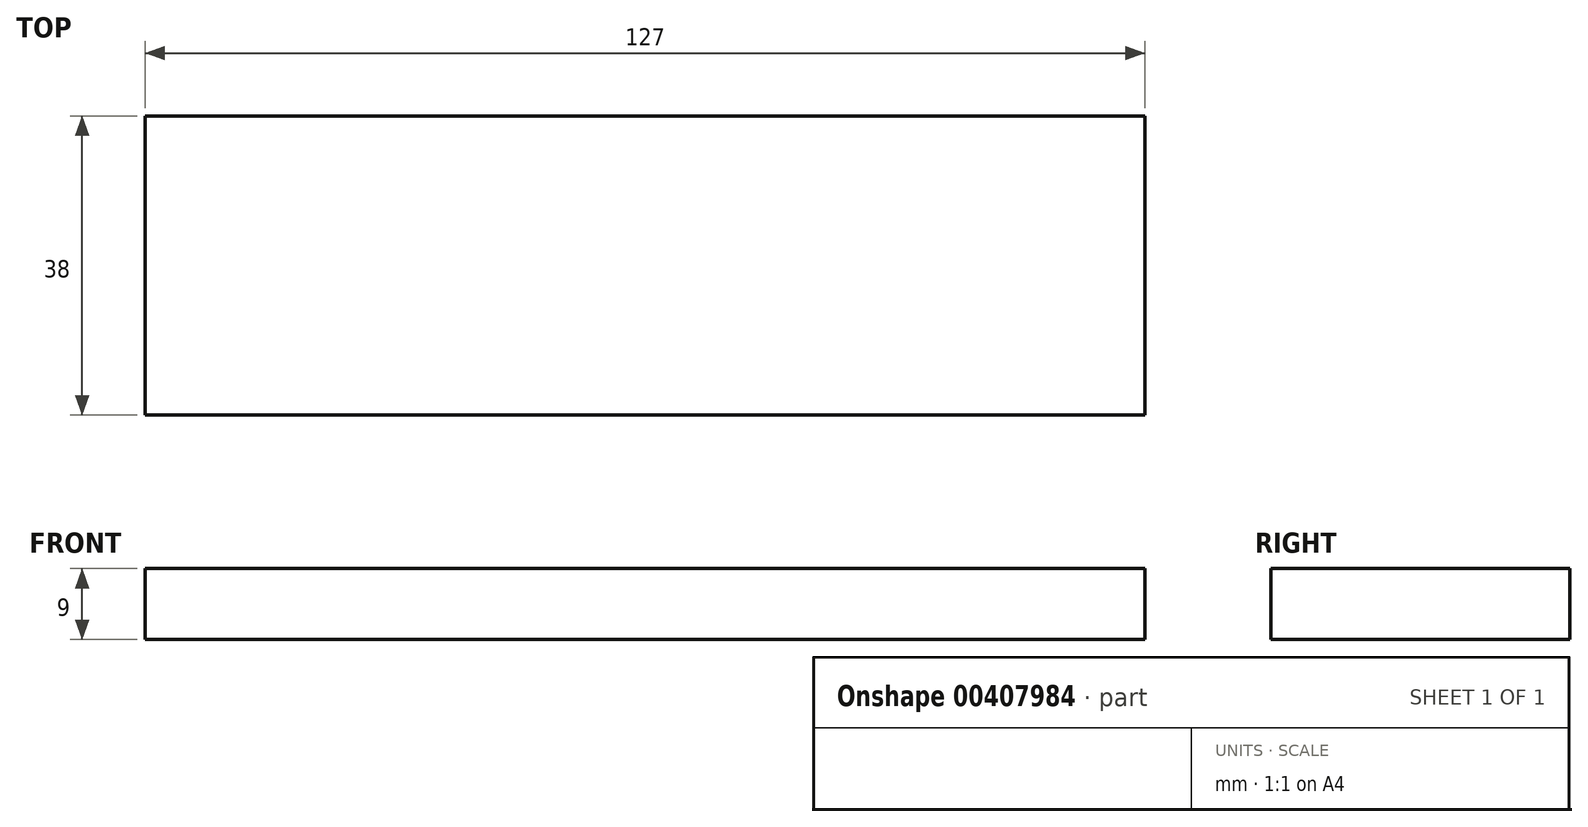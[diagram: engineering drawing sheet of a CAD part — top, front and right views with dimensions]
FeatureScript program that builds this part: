
annotation { "Feature Type Name" : "Feature", "Feature Type Description" : "" }
export const myFeature = defineFeature(function(context is Context, id is Id, definition is map)
    precondition{}
    {
        {
            var Q0;
            Q0=qCreatedBy(makeId("Top.planeOp"),FACE);
            var sketch = newSketch(context, id + "F0", { "sketchPlane" : qUnion([Q0])});
            skLineSegment(sketch, "E0.bottom", {"start": v(63.5, -19) * mm, "end": v(-63.5, -19) * mm});
            skLineSegment(sketch, "E0.top", {"start": v(63.5, 19) * mm, "end": v(-63.5, 19) * mm});
            skLineSegment(sketch, "E0.left", {"start": v(63.5, -19) * mm, "end": v(63.5, 19) * mm});
            skLineSegment(sketch, "E0.right", {"start": v(-63.5, -19) * mm, "end": v(-63.5, 19) * mm});
            skPoint(sketch, "E0.middle", {"position": v(0, 0) * mm});
            skSolve(sketch);
        }
        {
            var Q0;
            Q0 = qSketchRegion(id + "F0", true);
            extrude(context, id + "F1", {"entities" : qUnion([Q0]), "oppositeDirection" : true, "depth" : 9 * mm});
        }
    });
